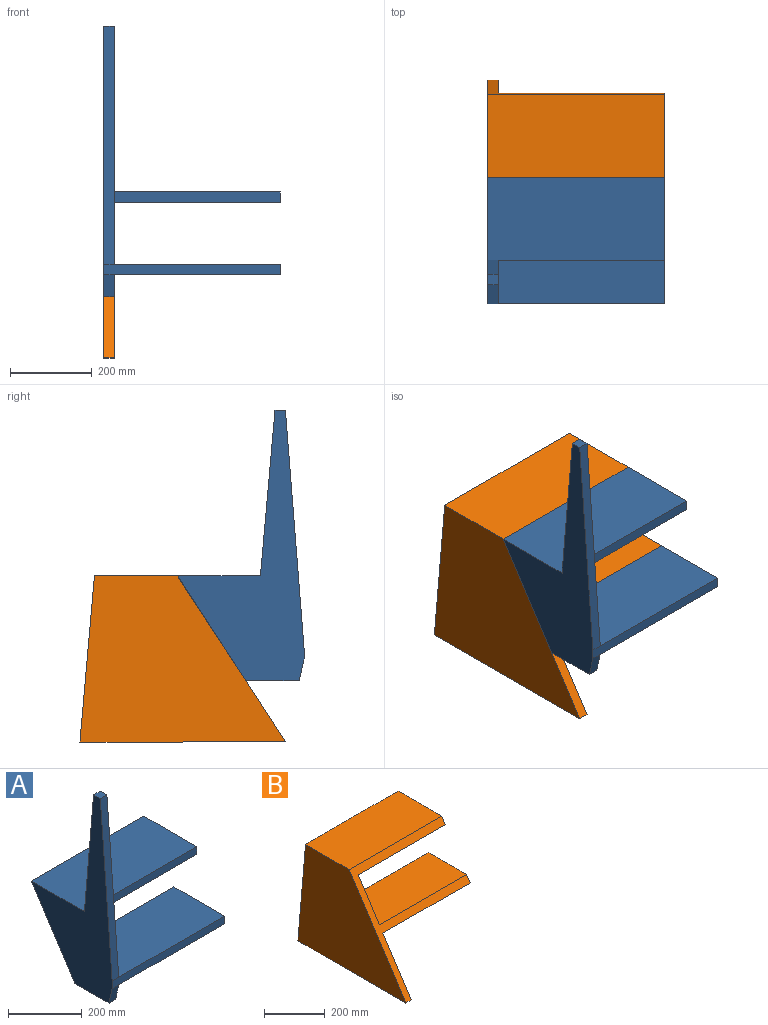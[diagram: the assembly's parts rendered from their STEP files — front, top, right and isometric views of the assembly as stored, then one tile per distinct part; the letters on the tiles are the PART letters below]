
ASSEMBLY  parts=2 mates=1
PART A: 17 faces, bbox 431.8x309.9x663.3 mm
  f0: plane 584.2x293.41mm, normal (1,0,0), area 62682.9mm2, adj f2,f4,f5,f6,f11,f12,f15
  f1: plane 177.8x53.73mm, normal (1,0,0), area 8290.4mm2, adj f2,f8,f9,f14
  f2: plane 431.8x256.93mm, normal (0,0.84,-0.55), area 32410.1mm2, adj f0,f1,f3,f9,f10,f12,f13,f14
  f3: plane 431.8x203.2mm, normal (0,0,1), area 87741.8mm2, adj f2,f4,f10,f11,f13
  f4: plane 406.4x35.56mm, normal (0,1,0.09), area 10362mm2, adj f0,f3,f5,f10
  f5: plane 25.5x25.4mm, normal (0,0,1), area 647.6mm2, adj f0,f4,f6,f10
  f6: plane 584.2x45.67mm, normal (0,-1,0.08), area 14884mm2, adj f0,f5,f7,f10
  f7: plane 431.8x25.4mm, normal (0,-1,0), area 10967.7mm2, adj f6,f8,f10,f14,f15,f16
  f8: plane 53.73x25.4mm, normal (0,-0.98,-0.22), area 1398.8mm2, adj f1,f7,f9,f10
  f9: plane 130.78x25.4mm, normal (0,0,-1), area 3321.9mm2, adj f1,f2,f8,f10
  f10: plane 663.33x309.93mm, normal (-1,0,0), area 80650.8mm2, adj f2,f3,f4,f5,f6,f7,f8,f9
  f11: plane 406.4x25.4mm, normal (0,-1,0), area 10322.6mm2, adj f0,f3,f12,f13
  f12: plane 406.4x186.68mm, normal (0,0,-1), area 75868.5mm2, adj f0,f2,f11,f13
  f13: plane 203.2x25.4mm, normal (1,0,0), area 4951.5mm2, adj f2,f3,f11,f12
  f14: plane 406.4x177.8mm, normal (0,0,-1), area 72257.9mm2, adj f1,f2,f7,f16
  f15: plane 406.4x194.32mm, normal (0,0,1), area 78969.9mm2, adj f0,f2,f7,f16
  f16: plane 194.32x25.4mm, normal (1,0,0), area 4725.9mm2, adj f2,f7,f14,f15
PART B: 12 faces, bbox 431.8x503x406.4 mm
  f0: plane 431.8x406.4mm, normal (0,-0.84,0.55), area 36938.6mm2, adj f1,f3,f4,f5,f6,f7,f8,f10
  f1: plane 503.01x25.4mm, normal (0,0,-1), area 12776.4mm2, adj f0,f2,f4,f5
  f2: plane 431.8x406.4mm, normal (0,1,0.09), area 20724mm2, adj f1,f3,f4,f5,f6,f7
  f3: plane 431.8x203.2mm, normal (0,0,1), area 87741.8mm2, adj f0,f2,f4,f7
  f4: plane 503.01x406.4mm, normal (-1,0,0), area 143501.4mm2, adj f0,f1,f2,f3
  f5: plane 503.01x381mm, normal (1,0,0), area 133376.3mm2, adj f0,f1,f2,f6,f8,f9,f10
  f6: plane 406.4x221.94mm, normal (0,0,-1), area 90195.6mm2, adj f0,f2,f5,f7
  f7: plane 221.94x25.4mm, normal (1,0,0), area 5399.3mm2, adj f0,f2,f3,f6
  f8: plane 406.4x194.32mm, normal (0,0,-1), area 78969.9mm2, adj f0,f5,f9,f11
  f9: plane 406.4x25.4mm, normal (0,1,0), area 10322.6mm2, adj f5,f8,f10,f11
  f10: plane 406.4x177.8mm, normal (0,0,1), area 72257.9mm2, adj f0,f5,f9,f11
  f11: plane 194.32x25.4mm, normal (1,0,0), area 4725.9mm2, adj f0,f8,f9,f10
PLACE A rot(axis=(1,0,0),0deg) t=(-608.86,322.62,112.41)mm
PLACE B t=(-608.86,322.62,112.41)mm fixed
MATE revolute B.f4 <-> A.f10  axis (1,0,0) through (-634.26,-199.74,518.81)mm
